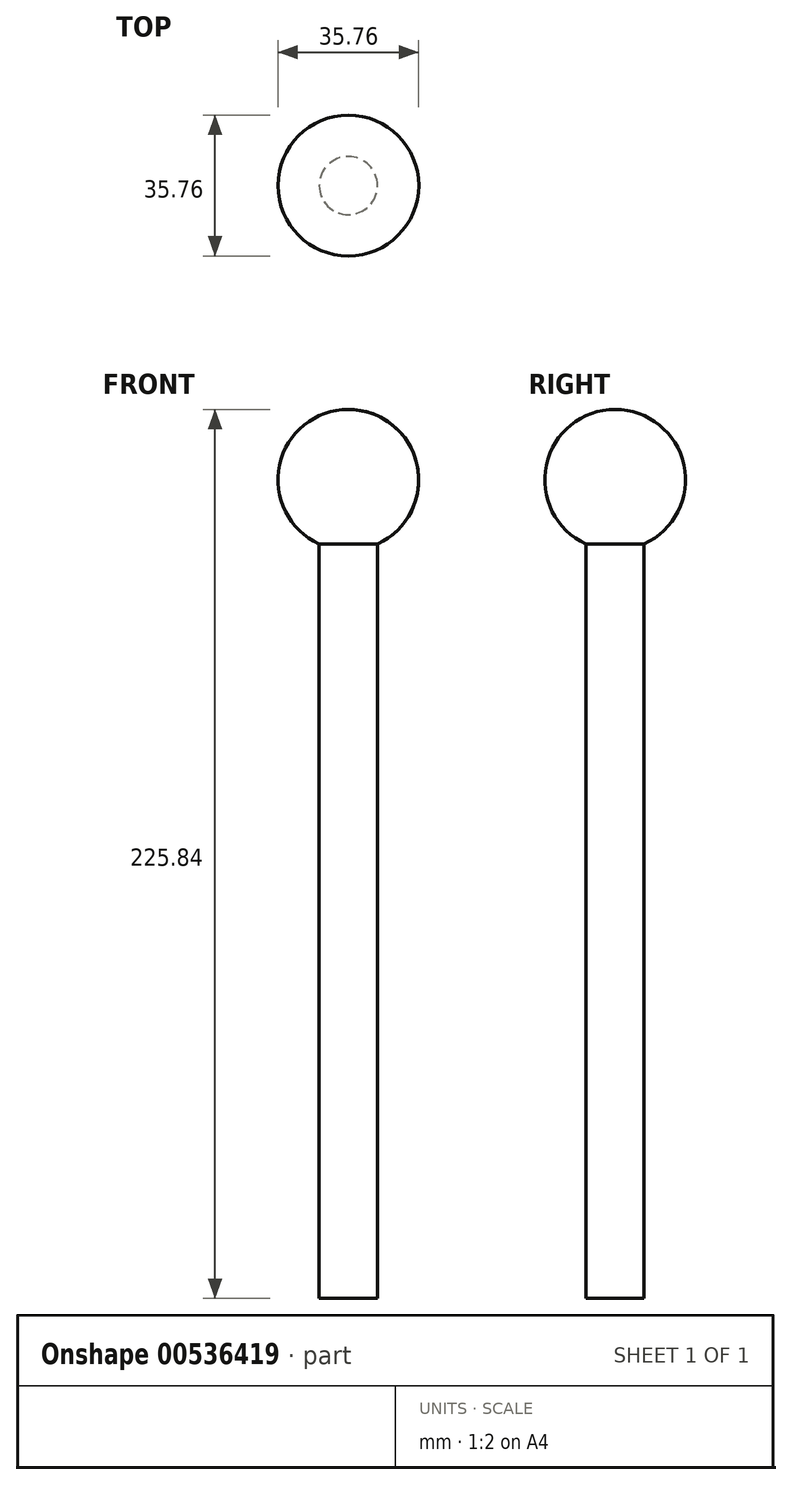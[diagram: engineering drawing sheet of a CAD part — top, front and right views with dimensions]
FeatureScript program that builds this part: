
annotation { "Feature Type Name" : "Feature", "Feature Type Description" : "" }
export const myFeature = defineFeature(function(context is Context, id is Id, definition is map)
    precondition{}
    {
        {
            var Q0;
            Q0=qCreatedBy(makeId("Front.planeOp"),FACE);
            var sketch = newSketch(context, id + "F0", { "sketchPlane" : qUnion([Q0])});
            skLineSegment(sketch, "E0.top", {"start": v(0, -165.58) * mm, "end": v(7.4, -165.58) * mm});
            skLineSegment(sketch, "E0.left", {"start": v(0, 34.06) * mm, "end": v(0, -165.58) * mm});
            skLineSegment(sketch, "E0.right", {"start": v(7.4, 26.1) * mm, "end": v(7.4, -165.58) * mm});
            skArc(sketch, "E1", {"start": v(7.4, 26.1) * mm, "mid": v(17.48, 46.16) * mm, "end": v(0, 60.26) * mm});
            skLineSegment(sketch, "E2", {"start": v(0, 34.06) * mm, "end": v(0, 60.26) * mm});
            skSolve(sketch);
        }
        {
            var Q0;
            Q0=makeQuery(id+"F0.imprint","IMPRINT",FACE,{"disambiguationData":[TD([[makeQuery(id+"F0.imprint","IMPRINT",EDGE,{"derivedFrom":sQuery(id+"F0.wireOp",EDGE,"E0.top")}),1.0]])]});
            var Q1;
            Q1=sQuery(id+"F0.wireOp",EDGE,"E2");
            revolve(context, id + "F1", {"entities" : qUnion([Q0]), "axis" : qUnion([Q1]), "revolveType" : RevolveType.FULL});
        }
    });
